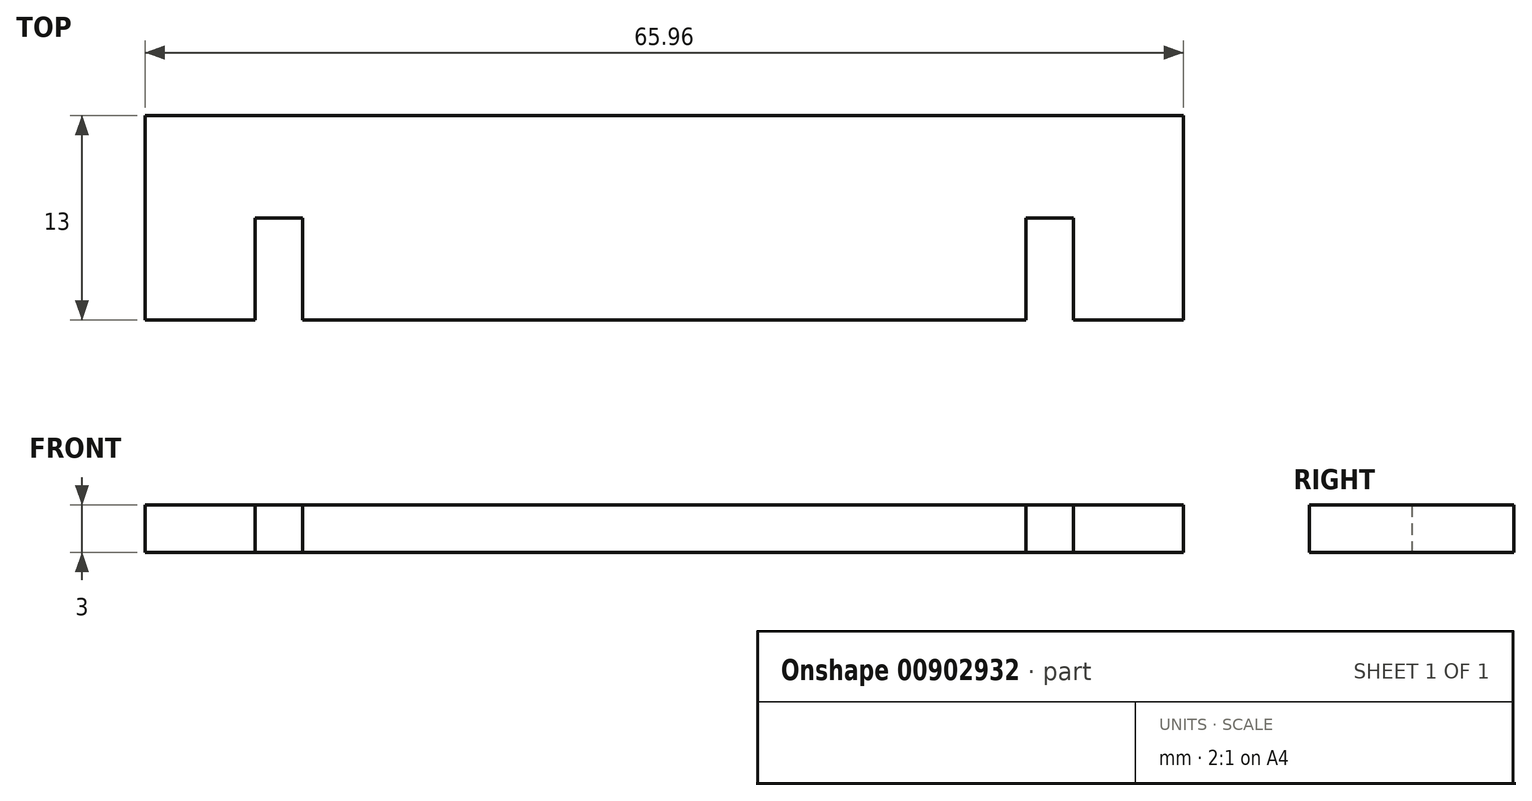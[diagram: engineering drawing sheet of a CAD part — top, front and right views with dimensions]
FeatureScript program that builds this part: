
annotation { "Feature Type Name" : "Feature", "Feature Type Description" : "" }
export const myFeature = defineFeature(function(context is Context, id is Id, definition is map)
    precondition{}
    {
        {
            var Q0;
            Q0=qCreatedBy(makeId("Top.planeOp"),FACE);
            var sketch = newSketch(context, id + "F0", { "sketchPlane" : qUnion([Q0])});
            skLineSegment(sketch, "E0.bottom", {"start": v(64.07, -55.45) * mm, "end": v(-20.43, -55.45) * mm});
            skLineSegment(sketch, "E0.top", {"start": v(64.07, -1.15) * mm, "end": v(-20.43, -1.15) * mm});
            skLineSegment(sketch, "E0.left", {"start": v(64.07, -55.45) * mm, "end": v(64.07, -1.15) * mm});
            skLineSegment(sketch, "E0.right", {"start": v(-20.43, -55.45) * mm, "end": v(-20.43, -1.15) * mm});
            skLineSegment(sketch, "E1.bottom", {"start": v(-20.43, -1.15) * mm, "end": v(-11.43, -1.15) * mm});
            skLineSegment(sketch, "E2.bottom", {"start": v(-11.43, -10.68) * mm, "end": v(-2.43, -10.68) * mm});
            skLineSegment(sketch, "E2.top", {"start": v(-11.43, -1.15) * mm, "end": v(-2.43, -1.15) * mm});
            skLineSegment(sketch, "E2.right", {"start": v(-2.43, -10.68) * mm, "end": v(-2.43, -1.15) * mm});
            skLineSegment(sketch, "E3.left", {"start": v(-11.43, -10.68) * mm, "end": v(-11.43, -45.91) * mm});
            skLineSegment(sketch, "E3.right", {"start": v(-20.43, -10.68) * mm, "end": v(-20.43, -45.91) * mm});
            skLineSegment(sketch, "E4.bottom", {"start": v(-11.43, -45.91) * mm, "end": v(54.53, -45.91) * mm});
            skLineSegment(sketch, "E4.top", {"start": v(-20.43, -55.45) * mm, "end": v(64.07, -55.45) * mm});
            skLineSegment(sketch, "E4.left", {"start": v(-20.43, -45.91) * mm, "end": v(-20.43, -55.45) * mm});
            skLineSegment(sketch, "E4.right", {"start": v(64.07, -45.91) * mm, "end": v(64.07, -55.45) * mm});
            skLineSegment(sketch, "E5", {"start": v(-2.43, -10.68) * mm, "end": v(54.53, -10.68) * mm});
            skLineSegment(sketch, "E6.bottom", {"start": v(64.07, -55.45) * mm, "end": v(54.53, -55.45) * mm});
            skLineSegment(sketch, "E6.top", {"start": v(64.07, -1.15) * mm, "end": v(54.53, -1.15) * mm});
            skLineSegment(sketch, "E6.right", {"start": v(54.53, -45.91) * mm, "end": v(54.53, -10.68) * mm});
            skLineSegment(sketch, "E7", {"start": v(-11.43, -23.68) * mm, "end": v(54.53, -23.68) * mm});
            skLineSegment(sketch, "E8.bottom", {"start": v(-20.43, -4.41) * mm, "end": v(-13.93, -4.41) * mm});
            skLineSegment(sketch, "E8.top", {"start": v(-20.43, -7.41) * mm, "end": v(-13.93, -7.41) * mm});
            skLineSegment(sketch, "E8.left", {"start": v(-20.43, -4.41) * mm, "end": v(-20.43, -7.41) * mm});
            skLineSegment(sketch, "E8.right", {"start": v(-13.93, -4.41) * mm, "end": v(-13.93, -7.41) * mm});
            skLineSegment(sketch, "E9.bottom", {"start": v(-20.43, -52.18) * mm, "end": v(-9.32, -52.18) * mm});
            skLineSegment(sketch, "E9.top", {"start": v(-20.43, -49.18) * mm, "end": v(-9.32, -49.18) * mm});
            skLineSegment(sketch, "E9.left", {"start": v(-20.43, -52.18) * mm, "end": v(-20.43, -49.18) * mm});
            skLineSegment(sketch, "E9.right", {"start": v(-9.32, -52.18) * mm, "end": v(-9.32, -49.18) * mm});
            skLineSegment(sketch, "E10.bottom", {"start": v(-4.43, -23.68) * mm, "end": v(-1.43, -23.68) * mm});
            skLineSegment(sketch, "E10.top", {"start": v(-4.43, -17.18) * mm, "end": v(-1.43, -17.18) * mm});
            skLineSegment(sketch, "E10.left", {"start": v(-4.43, -23.68) * mm, "end": v(-4.43, -17.18) * mm});
            skLineSegment(sketch, "E10.right", {"start": v(-1.43, -23.68) * mm, "end": v(-1.43, -17.18) * mm});
            skLineSegment(sketch, "E11.bottom", {"start": v(47.53, -23.68) * mm, "end": v(44.53, -23.68) * mm});
            skLineSegment(sketch, "E11.top", {"start": v(47.53, -17.18) * mm, "end": v(44.53, -17.18) * mm});
            skLineSegment(sketch, "E11.left", {"start": v(47.53, -23.68) * mm, "end": v(47.53, -17.18) * mm});
            skLineSegment(sketch, "E11.right", {"start": v(44.53, -23.68) * mm, "end": v(44.53, -17.18) * mm});
            skLineSegment(sketch, "E12.bottom", {"start": v(-1.43, -23.68) * mm, "end": v(-4.43, -23.68) * mm});
            skLineSegment(sketch, "E12.top", {"start": v(-1.43, -34.8) * mm, "end": v(-4.43, -34.8) * mm});
            skLineSegment(sketch, "E12.left", {"start": v(-1.43, -23.68) * mm, "end": v(-1.43, -34.8) * mm});
            skLineSegment(sketch, "E12.right", {"start": v(-4.43, -23.68) * mm, "end": v(-4.43, -34.8) * mm});
            skLineSegment(sketch, "E13.bottom", {"start": v(44.53, -23.68) * mm, "end": v(47.53, -23.68) * mm});
            skLineSegment(sketch, "E13.top", {"start": v(44.53, -34.8) * mm, "end": v(47.53, -34.8) * mm});
            skLineSegment(sketch, "E13.left", {"start": v(44.53, -23.68) * mm, "end": v(44.53, -34.8) * mm});
            skLineSegment(sketch, "E13.right", {"start": v(47.53, -23.68) * mm, "end": v(47.53, -34.8) * mm});
            skLineSegment(sketch, "E14.bottom", {"start": v(54.53, -45.91) * mm, "end": v(45.53, -45.91) * mm});
            skLineSegment(sketch, "E14.top", {"start": v(54.53, -55.45) * mm, "end": v(45.53, -55.45) * mm});
            skLineSegment(sketch, "E14.right", {"start": v(45.53, -45.91) * mm, "end": v(45.53, -55.45) * mm});
            skLineSegment(sketch, "E15.bottom", {"start": v(64.07, -4.41) * mm, "end": v(52.96, -4.41) * mm});
            skLineSegment(sketch, "E15.top", {"start": v(64.07, -7.41) * mm, "end": v(52.96, -7.41) * mm});
            skLineSegment(sketch, "E15.left", {"start": v(64.07, -4.41) * mm, "end": v(64.07, -7.41) * mm});
            skLineSegment(sketch, "E15.right", {"start": v(52.96, -4.41) * mm, "end": v(52.96, -7.41) * mm});
            skLineSegment(sketch, "E16.bottom", {"start": v(64.07, -49.18) * mm, "end": v(57.57, -49.18) * mm});
            skLineSegment(sketch, "E16.top", {"start": v(64.07, -52.18) * mm, "end": v(57.57, -52.18) * mm});
            skLineSegment(sketch, "E16.left", {"start": v(64.07, -49.18) * mm, "end": v(64.07, -52.18) * mm});
            skLineSegment(sketch, "E16.right", {"start": v(57.57, -49.18) * mm, "end": v(57.57, -52.18) * mm});
            skSolve(sketch);
        }
        {
            var Q0;
            {var subQ11=sQuery(id+"F0.wireOp",EDGE,"E2.bottom");Q0=makeQuery(id+"F0.imprint","IMPRINT",FACE,{"disambiguationData":[TD([[makeQuery(id+"F0.imprint","IMPRINT",EDGE,{"derivedFrom":subQ11}),-1.0]])]});}
            extrude(context, id + "F1", {"entities" : qUnion([Q0]), "depth" : 3 * mm, "offsetDistance" : 25 * mm});
        }
    });
